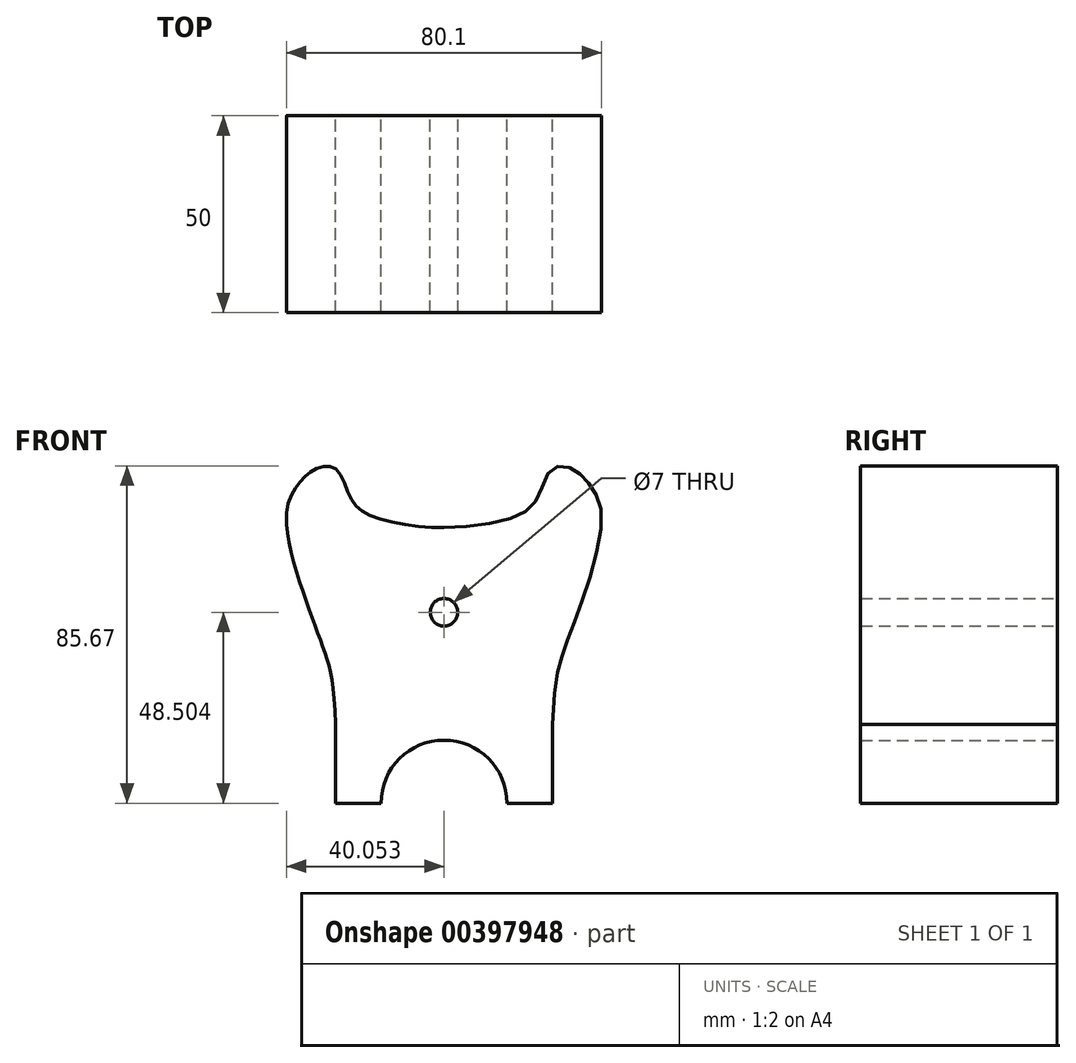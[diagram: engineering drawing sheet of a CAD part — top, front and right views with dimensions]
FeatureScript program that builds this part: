
annotation { "Feature Type Name" : "Feature", "Feature Type Description" : "" }
export const myFeature = defineFeature(function(context is Context, id is Id, definition is map)
    precondition{}
    {
        {
            var Q0;
            Q0=qCreatedBy(makeId("Front.planeOp"),FACE);
            var sketch = newSketch(context, id + "F0", { "sketchPlane" : qUnion([Q0])});
            skArc(sketch, "E0", {"start": v(18.92, 4.28) * mm, "mid": v(2.92, 20.28) * mm, "end": v(-13.08, 4.28) * mm});
            skLineSegment(sketch, "E1", {"start": v(2.92, 4.28) * mm, "end": v(2.92, 81.5) * mm, "construction": true});
            skLineSegment(sketch, "E2", {"start": v(-24.58, 24.28) * mm, "end": v(-24.58, 4.28) * mm});
            skLineSegment(sketch, "E3", {"start": v(-37.08, 77.99) * mm, "end": v(-37.08, 75.15) * mm});
            skFitSpline(sketch, "E4", {"points": [v(-24.58, 24.28) * mm, v(-27.42, 42.73) * mm, v(-32.66, 57.24) * mm, v(-37.08, 77.99) * mm, v(-33.86, 85.57) * mm, v(-29.55, 89.28) * mm, v(-24.58, 89.28) * mm, v(-20.95, 82.12) * mm, v(-15.02, 77.04) * mm, v(2.92, 74.28) * mm], "startDerivative": vector(-9.33, 219.79) * mm, "endDerivative": vector(119.38, -0.01) * mm});
            skFitSpline(sketch, "E5.MirrorCS", {"points": [v(30.42, 24.28) * mm, v(33.26, 42.73) * mm, v(38.5, 57.24) * mm, v(42.92, 77.99) * mm, v(39.7, 85.57) * mm, v(35.4, 89.28) * mm, v(30.42, 89.28) * mm, v(26.8, 82.12) * mm, v(20.87, 77.04) * mm, v(2.92, 74.28) * mm], "startDerivative": vector(9.33, 219.79) * mm, "endDerivative": vector(-119.38, -0.01) * mm});
            skLineSegment(sketch, "E6.MirrorCS", {"start": v(30.42, 24.28) * mm, "end": v(30.42, 4.28) * mm});
            skLineSegment(sketch, "E7", {"start": v(18.92, 4.28) * mm, "end": v(30.42, 4.28) * mm});
            skLineSegment(sketch, "E8", {"start": v(-13.08, 4.28) * mm, "end": v(-24.58, 4.28) * mm});
            skCircle(sketch, "E9", {"center": v(2.92, 52.78) * mm, "radius": 3.5 * mm});
            skSolve(sketch);
        }
        {
            var Q0;
            Q0 = qSketchRegion(id + "F0", true);
            extrude(context, id + "F1", {"entities" : qUnion([Q0]), "depth" : 50 * mm});
        }
    });
